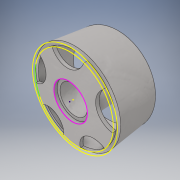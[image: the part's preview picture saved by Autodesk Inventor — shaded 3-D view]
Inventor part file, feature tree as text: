
AUTODESK INVENTOR PART (.ipt)
format: ipt  version: 2018 (Build 220112000, 112)  size: 180,736 bytes
history: native  units: in
note: dims shown in document units (in); Inventor stores cm internally (conversion verified against a paired STEP export)
features: sketch x5, projected_geometry x4, extrude x3
ambient origin geometry x8: Origin, YZ Plane, XZ Plane, XY Plane, X Axis, Y Axis, Z Axis, Center Point
bodies: Solid1 (feature_tree)
feature tree (12):
  extrude  "Extrusion1"  Depth=0.05in
  extrude  "Extrusion2"  Depth=0.05in
  sketch  "Sketch4"  dims[d4=0.57in d5=0.0in d6=0.05in d7=0.0in]
  sketch  "Sketch6"  dims[d11=1.9685in d13=360.0deg d15=0.05in d16=0.0in]
  sketch  "Sketch5"  dims[d10=0.25in]
  extrude  "Extrusion3"  Depth=0.05in TaperAngle=0.0deg
  sketch  "Sketch1"  dims[d0=0.44in d1=0.05in]
  sketch  "Sketch2"  dims[d2=0.35in d3=0.05in]
  projected_geometry  "Projected Loop1"
  projected_geometry  "Projected Loop2"
  projected_geometry  "Projected Loop3"
  projected_geometry  "Projected Loop4"
